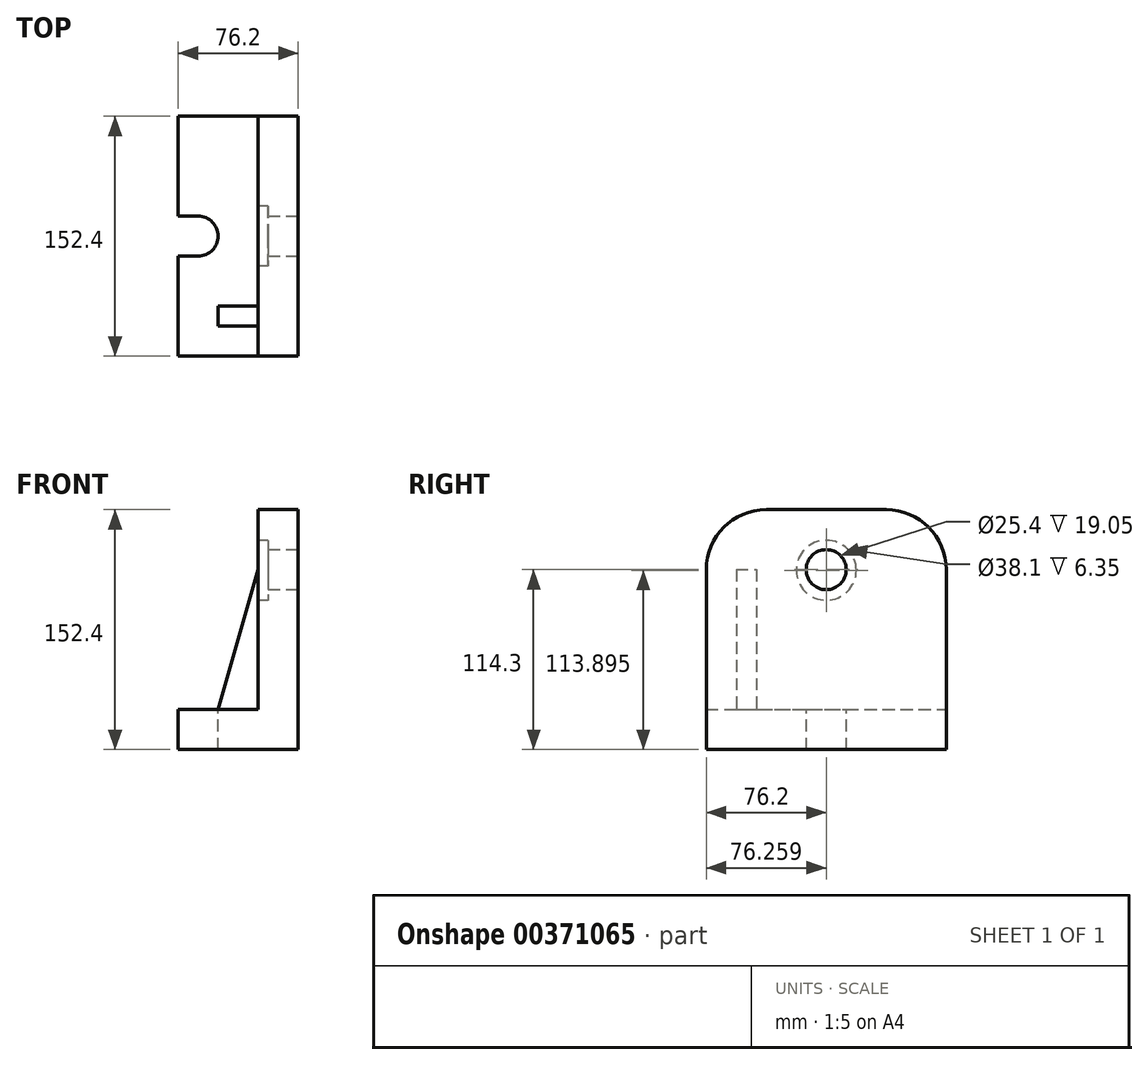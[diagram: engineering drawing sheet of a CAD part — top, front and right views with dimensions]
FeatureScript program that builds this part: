
annotation { "Feature Type Name" : "Feature", "Feature Type Description" : "" }
export const myFeature = defineFeature(function(context is Context, id is Id, definition is map)
    precondition{}
    {
        {
            var Q0;
            Q0=qCreatedBy(makeId("Front.planeOp"),FACE);
            var sketch = newSketch(context, id + "F0", { "sketchPlane" : qUnion([Q0])});
            skLineSegment(sketch, "E0", {"start": v(2.4, 183.42) * mm, "end": v(0, 183.42) * mm});
            skLineSegment(sketch, "E1", {"start": v(0, 0) * mm, "end": v(0, 152.4) * mm});
            skLineSegment(sketch, "E2", {"start": v(0, 152.4) * mm, "end": v(-25.4, 152.4) * mm});
            skLineSegment(sketch, "E3", {"start": v(-25.4, 152.4) * mm, "end": v(-25.4, 25.4) * mm});
            skLineSegment(sketch, "E4", {"start": v(-25.4, 25.4) * mm, "end": v(-76.2, 25.4) * mm});
            skLineSegment(sketch, "E5", {"start": v(-76.2, 25.4) * mm, "end": v(-76.2, 0) * mm});
            skLineSegment(sketch, "E6", {"start": v(-76.2, 0) * mm, "end": v(0, 0) * mm});
            skSolve(sketch);
        }
        {
            var Q0;
            Q0=makeQuery(id+"F0.imprint","IMPRINT",FACE,{"disambiguationData":[TD([[makeQuery(id+"F0.imprint","IMPRINT",EDGE,{"derivedFrom":sQuery(id+"F0.wireOp",EDGE,"E1")}),1.0]])]});
            extrude(context, id + "F1", {"entities" : qUnion([Q0]), "endBound" : BoundingType.SYMMETRIC, "depth" : 152.4 * mm});
        }
        {
            var Q0;
            Q0=qCreatedBy(makeId("Right.planeOp"),FACE);
            var sketch = newSketch(context, id + "F2", { "sketchPlane" : qUnion([Q0])});
            skCircle(sketch, "E7", {"center": v(0, 114.3) * mm, "radius": 12.7 * mm});
            skSolve(sketch);
        }
        {
            var Q0;
            Q0=makeQuery(id+"F2.imprint","IMPRINT",FACE,{"disambiguationData":[TD([[makeQuery(id+"F2.imprint","IMPRINT",EDGE,{"derivedFrom":sQuery(id+"F2.wireOp",EDGE,"E7")}),1.0]])]});
            extrude(context, id + "F3", {"entities" : qUnion([Q0]), "operationType" : NewBodyOperationType.REMOVE, "endBound" : BoundingType.THROUGH_ALL, "oppositeDirection" : true, "depth" : 25.4 * mm});
        }
        {
            var Q0;
            Q0=makeQuery(id+"F1.opExtrude","SWEPT_FACE",FACE,{"disambiguationData":[OSD([sQuery(id+"F0.wireOp",EDGE,"E4")])]});
            var sketch = newSketch(context, id + "F4", { "sketchPlane" : qUnion([Q0])});
            skArc(sketch, "E8", {"start": v(-50.8, 0) * mm, "mid": v(-54.52, 8.98) * mm, "end": v(-63.5, 12.7) * mm});
            skArc(sketch, "E9", {"start": v(-50.8, 0) * mm, "mid": v(-54.52, -8.98) * mm, "end": v(-63.5, -12.7) * mm});
            skLineSegment(sketch, "E10", {"start": v(-63.5, 12.7) * mm, "end": v(-76.2, 12.7) * mm});
            skLineSegment(sketch, "E11", {"start": v(-63.5, -12.7) * mm, "end": v(-76.2, -12.7) * mm});
            skSolve(sketch);
        }
        {
            var Q0;
            Q0=makeQuery(id+"F4.imprint","IMPRINT",FACE,{"disambiguationData":[TD([[makeQuery(id+"F4.imprint","IMPRINT",EDGE,{"derivedFrom":sQuery(id+"F4.wireOp",EDGE,"E8")}),1.0]])]});
            extrude(context, id + "F5", {"entities" : qUnion([Q0]), "operationType" : NewBodyOperationType.REMOVE, "oppositeDirection" : true, "depth" : 46.74 * mm});
        }
        {
            var Q0;
            Q0=makeQuery(id+"F1.opExtrude","SWEPT_FACE",FACE,{"disambiguationData":[OSD([sQuery(id+"F0.wireOp",EDGE,"E3")])]});
            var sketch = newSketch(context, id + "F6", { "sketchPlane" : qUnion([Q0])});
            skCircle(sketch, "E12", {"center": v(-0.06, 113.9) * mm, "radius": 19.05 * mm});
            skPoint(sketch, "E12.first.point", {"position": v(0, 132.94) * mm});
            skPoint(sketch, "E12.second.point", {"position": v(0, 94.84) * mm});
            skPoint(sketch, "E12.third.point", {"position": v(-16.04, 103.53) * mm});
            skSolve(sketch);
        }
        {
            var Q0;
            Q0=qSketchRegion(id+"F6",true);
            extrude(context, id + "F7", {"entities" : qUnion([Q0]), "operationType" : NewBodyOperationType.REMOVE, "oppositeDirection" : true, "depth" : 6.35 * mm});
        }
        {
            var Q0;
            Q0=makeQuery(id+"F1.opExtrude","CAP_EDGE",EDGE,{"disambiguationData":[OSD([sQuery(id+"F0.wireOp",EDGE,"E2")])],"isStart":true});
            var Q1;
            Q1=makeQuery(id+"F1.opExtrude","CAP_EDGE",EDGE,{"disambiguationData":[OSD([sQuery(id+"F0.wireOp",EDGE,"E2")])],"isStart":false});
            fillet(context, id + "F8", {"entities" : qUnion([Q0, Q1]), "radius" : 38.1 * mm, "tangentPropagation" : true, "allowEdgeOverflow" : false});
        }
        {
            var Q0;
            Q0=qCreatedBy(makeId("Front.planeOp"),FACE);
            cPlane(context, id + "F9", {"entities" : qUnion([Q0]), "cplaneType" : CPlaneType.OFFSET, "offset" : 44.45 * mm, "width" : 152.4 * mm, "height" : 152.4 * mm});
        }
        {
            var Q0;
            Q0=qCreatedBy(id+"F9.planeOp",FACE);
            var sketch = newSketch(context, id + "F10", { "sketchPlane" : qUnion([Q0])});
            skPoint(sketch, "E13.0", {"position": v(-25.4, 25.4) * mm});
            skLineSegment(sketch, "E14.0", {"start": v(-25.4, 114.3) * mm, "end": v(-25.4, 25.4) * mm});
            skLineSegment(sketch, "E15", {"start": v(-50.8, 25.4) * mm, "end": v(-25.4, 114.3) * mm});
            skLineSegment(sketch, "E16", {"start": v(-50.8, 25.4) * mm, "end": v(-25.4, 25.4) * mm});
            skSolve(sketch);
        }
        {
            var Q0;
            Q0=qSketchRegion(id+"F10",true);
            extrude(context, id + "F11", {"entities" : qUnion([Q0]), "operationType" : NewBodyOperationType.ADD, "depth" : 12.7 * mm});
        }
    });
